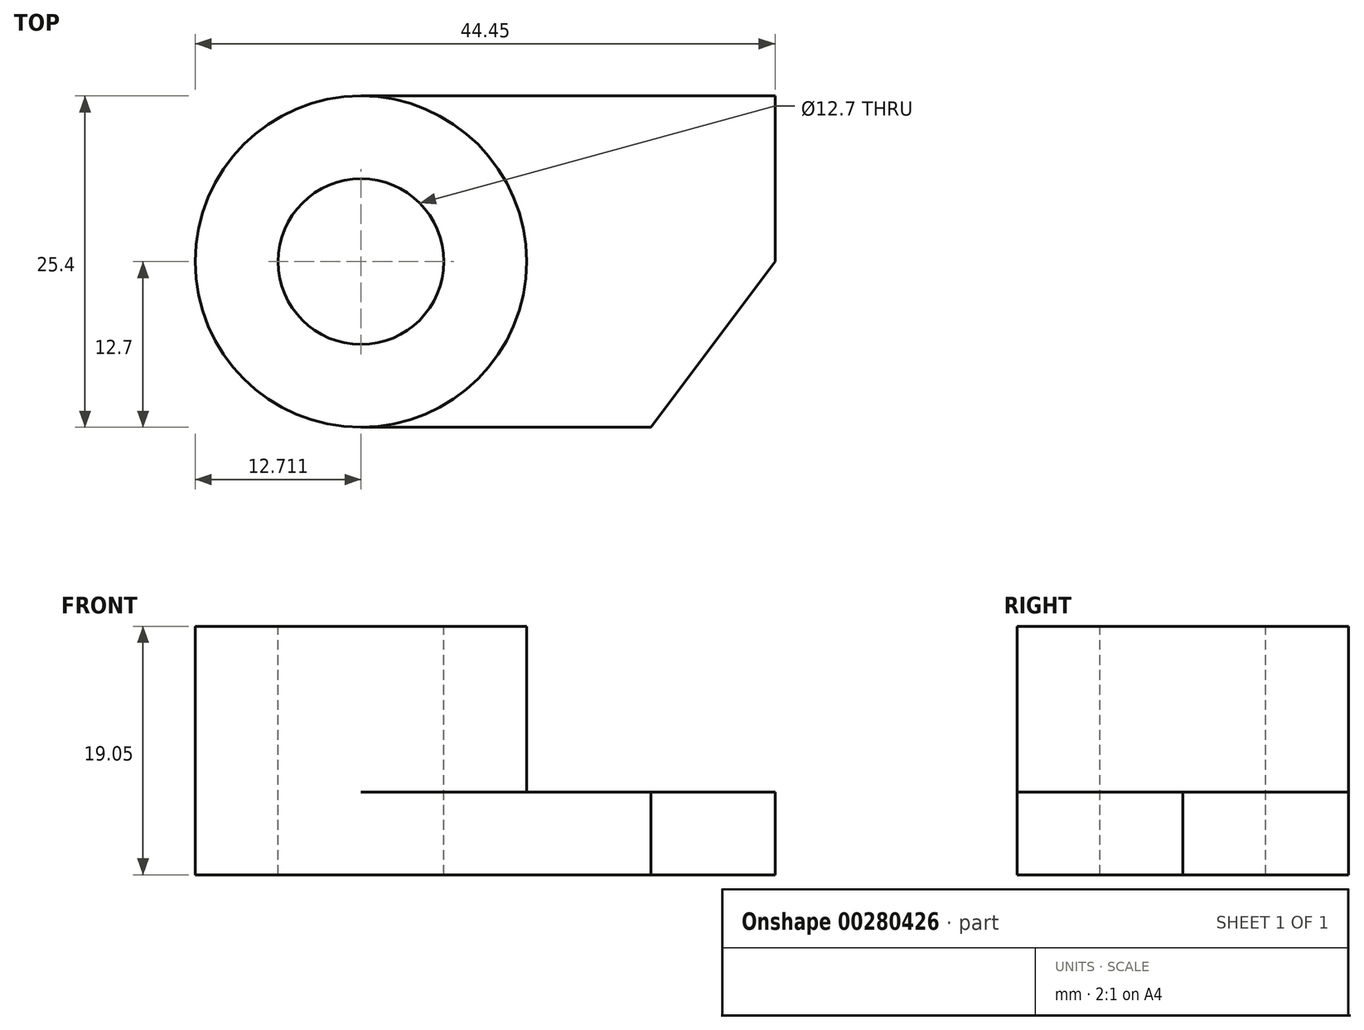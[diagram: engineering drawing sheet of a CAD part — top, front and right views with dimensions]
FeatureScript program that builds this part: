
annotation { "Feature Type Name" : "Feature", "Feature Type Description" : "" }
export const myFeature = defineFeature(function(context is Context, id is Id, definition is map)
    precondition{}
    {
        {
            var Q0;
            Q0=qCreatedBy(makeId("Front.planeOp"),FACE);
            var sketch = newSketch(context, id + "F0", { "sketchPlane" : qUnion([Q0])});
            skLineSegment(sketch, "E0", {"start": v(0, 0) * mm, "end": v(44.45, 0) * mm});
            skLineSegment(sketch, "E1", {"start": v(44.45, 0) * mm, "end": v(44.45, 6.35) * mm});
            skLineSegment(sketch, "E2", {"start": v(44.45, 6.35) * mm, "end": v(25.4, 6.35) * mm});
            skLineSegment(sketch, "E3", {"start": v(25.4, 6.35) * mm, "end": v(25.4, 19.05) * mm});
            skLineSegment(sketch, "E4", {"start": v(25.4, 19.05) * mm, "end": v(0, 19.05) * mm});
            skLineSegment(sketch, "E5", {"start": v(0, 19.05) * mm, "end": v(0, 0) * mm});
            skSolve(sketch);
        }
        {
            var Q0;
            Q0 = qSketchRegion(id + "F0", true);
            extrude(context, id + "F1", {"entities" : qUnion([Q0]), "depth" : 25.4 * mm, "symmetric" : true});
        }
        {
            var Q0;
            Q0=makeQuery(id+"F1.opExtrude","SWEPT_FACE",FACE,{"disambiguationData":[OSD([sQuery(id+"F0.wireOp",EDGE,"E2")])]});
            var sketch = newSketch(context, id + "F2", { "sketchPlane" : qUnion([Q0])});
            skLineSegment(sketch, "E6", {"start": v(44.45, -12.7) * mm, "end": v(34.93, -12.7) * mm});
            skLineSegment(sketch, "E7", {"start": v(34.93, -12.7) * mm, "end": v(44.45, 0) * mm});
            skSolve(sketch);
        }
        {
            var Q0;
            {var subQ0=sQuery(id+"F2.wireOp",EDGE,"E6");Q0=makeQuery(id+"F2.imprint","IMPRINT",FACE,{"disambiguationData":[TD([[makeQuery(id+"F2.imprint","IMPRINT",EDGE,{"derivedFrom":subQ0}),-1.0]])]});}
            extrude(context, id + "F3", {"entities" : qUnion([Q0]), "operationType" : NewBodyOperationType.REMOVE, "endBound" : BoundingType.THROUGH_ALL, "oppositeDirection" : true, "depth" : 25.4 * mm});
        }
        {
            var Q0;
            Q0=makeQuery(id+"F1.opExtrude","SWEPT_FACE",FACE,{"disambiguationData":[OSD([sQuery(id+"F0.wireOp",EDGE,"E4")])]});
            var sketch = newSketch(context, id + "F4", { "sketchPlane" : qUnion([Q0])});
            skPoint(sketch, "E8.endSnap0", {"position": v(25.4, 0) * mm});
            skCircle(sketch, "E9", {"center": v(12.71, 0) * mm, "radius": 6.35 * mm});
            skSolve(sketch);
        }
        {
            var Q0;
            Q0=makeQuery(id+"F4.imprint","IMPRINT",FACE,{"disambiguationData":[TD([[makeQuery(id+"F4.imprint","IMPRINT",EDGE,{"derivedFrom":sQuery(id+"F4.wireOp",EDGE,"E9")}),1.0]])]});
            extrude(context, id + "F5", {"entities" : qUnion([Q0]), "operationType" : NewBodyOperationType.REMOVE, "endBound" : BoundingType.THROUGH_ALL, "oppositeDirection" : true, "depth" : 25.4 * mm});
        }
        {
            var Q0;
            Q0=makeQuery(id+"F1.opExtrude","CAP_EDGE",EDGE,{"disambiguationData":[OSD([sQuery(id+"F0.wireOp",EDGE,"E5")])],"isStart":false});
            fillet(context, id + "F6", {"entities" : qUnion([Q0]), "radius" : 12.7 * mm, "tangentPropagation" : true, "allowEdgeOverflow" : false});
        }
        {
            var Q0;
            Q0=makeQuery(id+"F1.opExtrude","CAP_EDGE",EDGE,{"disambiguationData":[OSD([sQuery(id+"F0.wireOp",EDGE,"E5")])],"isStart":true});
            fillet(context, id + "F7", {"entities" : qUnion([Q0]), "radius" : 12.7 * mm, "tangentPropagation" : true, "allowEdgeOverflow" : false});
        }
        {
            var Q0;
            Q0=makeQuery(id+"F1.opExtrude","CAP_EDGE",EDGE,{"disambiguationData":[OSD([sQuery(id+"F0.wireOp",EDGE,"E3")])],"isStart":false});
            fillet(context, id + "F8", {"entities" : qUnion([Q0]), "radius" : 12.7 * mm, "tangentPropagation" : true, "allowEdgeOverflow" : false});
        }
        {
            var Q0;
            Q0=makeQuery(id+"F1.opExtrude","CAP_EDGE",EDGE,{"disambiguationData":[OSD([sQuery(id+"F0.wireOp",EDGE,"E3")])],"isStart":true});
            fillet(context, id + "F9", {"entities" : qUnion([Q0]), "radius" : 12.7 * mm, "tangentPropagation" : true, "allowEdgeOverflow" : false});
        }
    });
